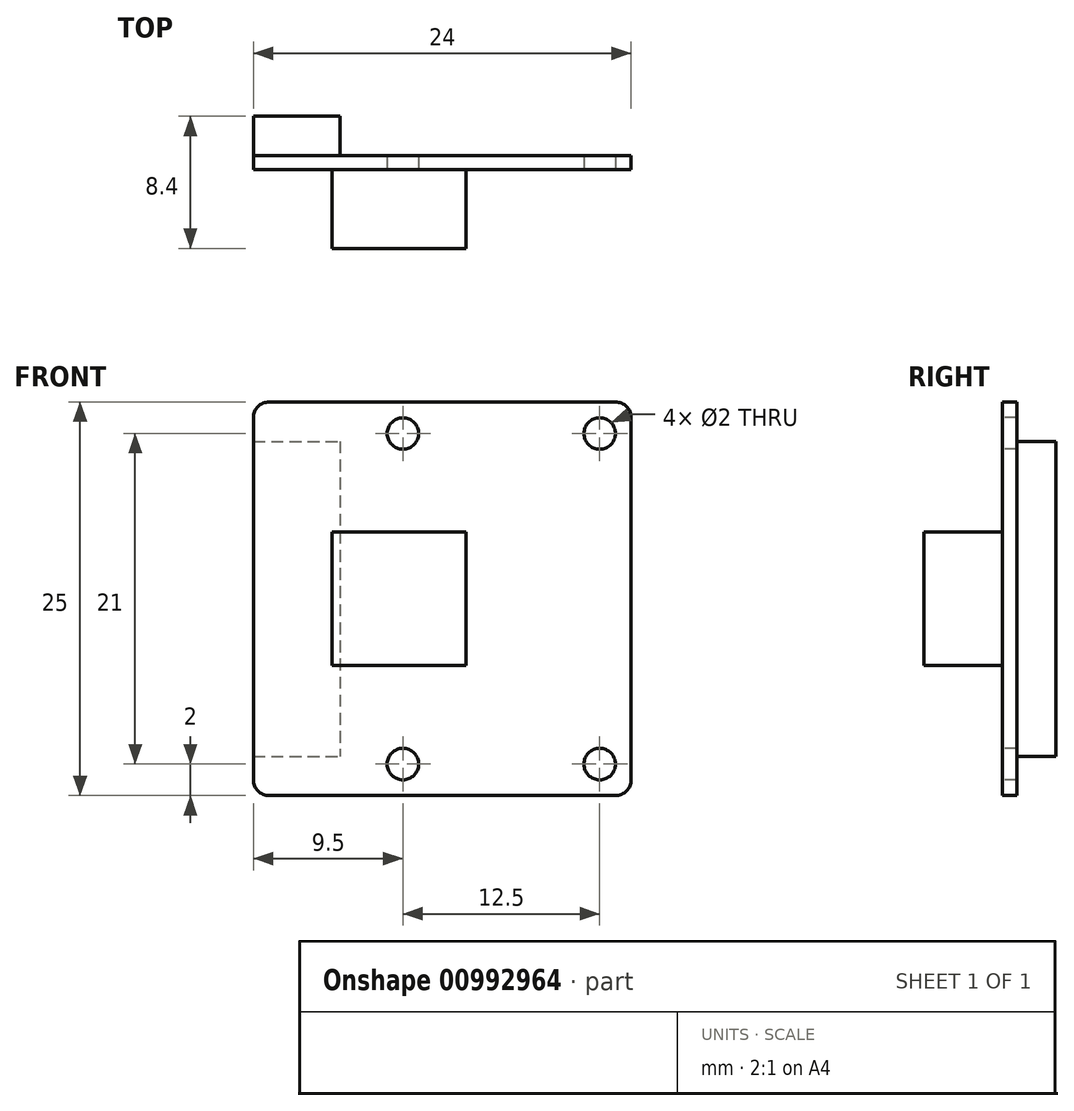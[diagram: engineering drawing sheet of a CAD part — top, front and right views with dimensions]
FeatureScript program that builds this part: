
annotation { "Feature Type Name" : "Feature", "Feature Type Description" : "" }
export const myFeature = defineFeature(function(context is Context, id is Id, definition is map)
    precondition{}
    {
        {
            var Q0;
            Q0=qCreatedBy(makeId("Front.planeOp"),FACE);
            var sketch = newSketch(context, id + "F0", { "sketchPlane" : qUnion([Q0])});
            skLineSegment(sketch, "E0.bottom", {"start": v(12, 12.5) * mm, "end": v(-12, 12.5) * mm});
            skLineSegment(sketch, "E0.top", {"start": v(12, -12.5) * mm, "end": v(-12, -12.5) * mm});
            skLineSegment(sketch, "E0.left", {"start": v(12, 12.5) * mm, "end": v(12, -12.5) * mm});
            skLineSegment(sketch, "E0.right", {"start": v(-12, 12.5) * mm, "end": v(-12, -12.5) * mm});
            skPoint(sketch, "E0.middle", {"position": v(0, 0) * mm});
            skSolve(sketch);
        }
        {
            var Q0;
            Q0 = qSketchRegion(id + "F0", true);
            extrude(context, id + "F1", {"entities" : qUnion([Q0]), "depth" : 0.9 * mm, "offsetDistance" : 25.4 * mm});
        }
        {
            var Q0;
            Q0=makeQuery(id+"F1.opExtrude","SWEPT_EDGE",EDGE,{"disambiguationData":[OSD([sQuery(id+"F0.wireOp",EDGE,"E0.bottom"),sQuery(id+"F0.wireOp",EDGE,"E0.left")])]});
            var Q1;
            Q1=makeQuery(id+"F1.opExtrude","SWEPT_EDGE",EDGE,{"disambiguationData":[OSD([sQuery(id+"F0.wireOp",EDGE,"E0.top"),sQuery(id+"F0.wireOp",EDGE,"E0.left")])]});
            var Q2;
            Q2=makeQuery(id+"F1.opExtrude","SWEPT_EDGE",EDGE,{"disambiguationData":[OSD([sQuery(id+"F0.wireOp",EDGE,"E0.top"),sQuery(id+"F0.wireOp",EDGE,"E0.right")])]});
            var Q3;
            Q3=makeQuery(id+"F1.opExtrude","SWEPT_EDGE",EDGE,{"disambiguationData":[OSD([sQuery(id+"F0.wireOp",EDGE,"E0.bottom"),sQuery(id+"F0.wireOp",EDGE,"E0.right")])]});
            fillet(context, id + "F2", {"entities" : qUnion([Q0, Q1, Q2, Q3]), "radius" : 1 * mm, "tangentPropagation" : true, "allowEdgeOverflow" : false});
        }
        {
            var Q0;
            Q0=makeQuery(id+"F1.opExtrude","CAP_FACE",FACE,{"disambiguationData":[OSD([sQuery(id+"F0.wireOp",EDGE,"E0.bottom"),sQuery(id+"F0.wireOp",EDGE,"E0.top"),sQuery(id+"F0.wireOp",EDGE,"E0.left"),sQuery(id+"F0.wireOp",EDGE,"E0.right")])],"isStart":false});
            var sketch = newSketch(context, id + "F3", { "sketchPlane" : qUnion([Q0])});
            skLineSegment(sketch, "E1.bottom", {"start": v(1.5, 4.25) * mm, "end": v(-7, 4.25) * mm});
            skLineSegment(sketch, "E1.top", {"start": v(1.5, -4.25) * mm, "end": v(-7, -4.25) * mm});
            skLineSegment(sketch, "E1.left", {"start": v(1.5, 4.25) * mm, "end": v(1.5, -4.25) * mm});
            skLineSegment(sketch, "E1.right", {"start": v(-7, 4.25) * mm, "end": v(-7, -4.25) * mm});
            skPoint(sketch, "E1.middle", {"position": v(-2.75, 0) * mm});
            skSolve(sketch);
        }
        {
            var Q0;
            Q0 = qSketchRegion(id + "F3", true);
            extrude(context, id + "F4", {"entities" : qUnion([Q0]), "operationType" : NewBodyOperationType.ADD, "depth" : 5 * mm, "offsetDistance" : 25.4 * mm});
        }
        {
            var Q0;
            Q0=makeQuery(id+"F1.opExtrude","CAP_FACE",FACE,{"disambiguationData":[OSD([sQuery(id+"F0.wireOp",EDGE,"E0.bottom"),sQuery(id+"F0.wireOp",EDGE,"E0.top"),sQuery(id+"F0.wireOp",EDGE,"E0.left"),sQuery(id+"F0.wireOp",EDGE,"E0.right")])],"isStart":false});
            var sketch = newSketch(context, id + "F5", { "sketchPlane" : qUnion([Q0])});
            skCircle(sketch, "E2", {"center": v(10, 10.5) * mm, "radius": 1 * mm});
            skCircle(sketch, "E3", {"center": v(-2.5, 10.5) * mm, "radius": 1 * mm});
            skCircle(sketch, "E4.MirrorC", {"center": v(-2.5, -10.5) * mm, "radius": 1 * mm});
            skCircle(sketch, "E5.MirrorC", {"center": v(10, -10.5) * mm, "radius": 1 * mm});
            skSolve(sketch);
        }
        {
            var Q0;
            Q0 = qSketchRegion(id + "F5", true);
            extrude(context, id + "F6", {"entities" : qUnion([Q0]), "operationType" : NewBodyOperationType.REMOVE, "endBound" : BoundingType.THROUGH_ALL, "oppositeDirection" : true, "depth" : 25.4 * mm, "offsetDistance" : 25.4 * mm});
        }
        {
            var Q0;
            Q0=makeQuery(id+"F1.opExtrude","CAP_FACE",FACE,{"disambiguationData":[OSD([sQuery(id+"F0.wireOp",EDGE,"E0.bottom"),sQuery(id+"F0.wireOp",EDGE,"E0.top"),sQuery(id+"F0.wireOp",EDGE,"E0.left"),sQuery(id+"F0.wireOp",EDGE,"E0.right")])],"isStart":true});
            var sketch = newSketch(context, id + "F7", { "sketchPlane" : qUnion([Q0])});
            skLineSegment(sketch, "E6.bottom", {"start": v(12, 10) * mm, "end": v(6.5, 10) * mm});
            skLineSegment(sketch, "E6.top", {"start": v(12, -10) * mm, "end": v(6.5, -10) * mm});
            skLineSegment(sketch, "E6.left", {"start": v(12, 10) * mm, "end": v(12, -10) * mm});
            skLineSegment(sketch, "E6.right", {"start": v(6.5, 10) * mm, "end": v(6.5, -10) * mm});
            skPoint(sketch, "E6.middle", {"position": v(9.25, 0) * mm});
            skSolve(sketch);
        }
        {
            var Q0;
            Q0 = qSketchRegion(id + "F7", true);
            extrude(context, id + "F8", {"entities" : qUnion([Q0]), "operationType" : NewBodyOperationType.ADD, "depth" : 2.5 * mm, "offsetDistance" : 25.4 * mm});
        }
    });
